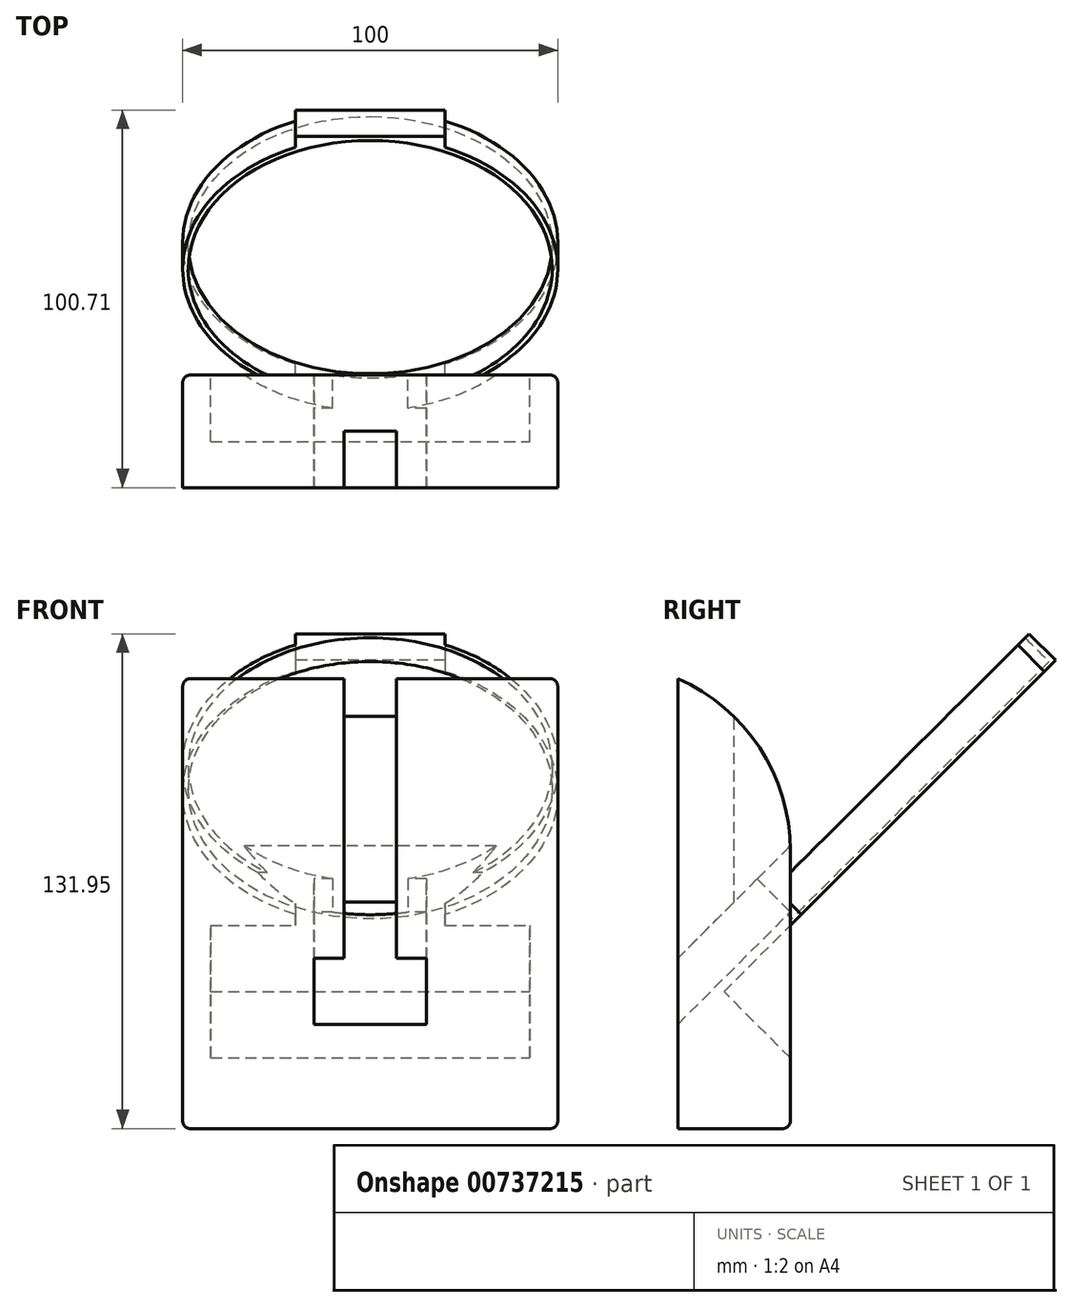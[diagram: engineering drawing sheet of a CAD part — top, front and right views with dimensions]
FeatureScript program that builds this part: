
annotation { "Feature Type Name" : "Feature", "Feature Type Description" : "" }
export const myFeature = defineFeature(function(context is Context, id is Id, definition is map)
    precondition{}
    {
        {
            var Q0;
            Q0=qCreatedBy(makeId("Front.planeOp"),FACE);
            var sketch = newSketch(context, id + "F0", { "sketchPlane" : qUnion([Q0])});
            skLineSegment(sketch, "E0.bottom", {"start": v(50, -60) * mm, "end": v(-50, -60) * mm});
            skLineSegment(sketch, "E0.top", {"start": v(50, 60) * mm, "end": v(-50, 60) * mm});
            skLineSegment(sketch, "E0.left", {"start": v(50, -60) * mm, "end": v(50, 60) * mm});
            skLineSegment(sketch, "E0.right", {"start": v(-50, -60) * mm, "end": v(-50, 60) * mm});
            skPoint(sketch, "E0.middle", {"position": v(0, 0) * mm});
            skSolve(sketch);
        }
        {
            var Q0;
            Q0 = qSketchRegion(id + "F0", true);
            extrude(context, id + "F1", {"entities" : qUnion([Q0]), "depth" : 30 * mm, "offsetDistance" : 25 * mm});
        }
        {
            var Q0;
            Q0=qCreatedBy(makeId("Right.planeOp"),FACE);
            var sketch = newSketch(context, id + "F2", { "sketchPlane" : qUnion([Q0])});
            skLineSegment(sketch, "E1", {"start": v(0, 8.31) * mm, "end": v(63.64, 71.95) * mm});
            skLineSegment(sketch, "E2", {"start": v(63.64, 71.95) * mm, "end": v(70.71, 64.88) * mm});
            skLineSegment(sketch, "E3", {"start": v(70.71, 64.88) * mm, "end": v(0, -5.83) * mm});
            skLineSegment(sketch, "E4", {"start": v(0, -5.83) * mm, "end": v(0, 8.31) * mm});
            skLineSegment(sketch, "E5", {"start": v(0, -5.83) * mm, "end": v(-17.68, -23.5) * mm});
            skLineSegment(sketch, "E6", {"start": v(-17.68, -23.5) * mm, "end": v(0, -41.19) * mm});
            skLineSegment(sketch, "E7", {"start": v(0, -41.19) * mm, "end": v(0, -5.83) * mm});
            skSolve(sketch);
        }
        {
            var Q0;
            Q0=makeQuery(id+"F2.imprint","IMPRINT",FACE,{"disambiguationData":[TD([[makeQuery(id+"F2.imprint","IMPRINT",EDGE,{"derivedFrom":sQuery(id+"F2.wireOp",EDGE,"E1")}),-1.0]])]});
            extrude(context, id + "F3", {"entities" : qUnion([Q0]), "operationType" : NewBodyOperationType.ADD, "endBound" : BoundingType.SYMMETRIC, "depth" : 40 * mm, "offsetDistance" : 25 * mm});
        }
        {
            var Q0;
            Q0=qCreatedBy(makeId("Right.planeOp"),FACE);
            var sketch = newSketch(context, id + "F4", { "sketchPlane" : qUnion([Q0])});
            skLineSegment(sketch, "E8", {"start": v(0, -41.19) * mm, "end": v(-17.68, -23.5) * mm});
            skLineSegment(sketch, "E9", {"start": v(-17.68, -23.5) * mm, "end": v(0, -5.83) * mm});
            skLineSegment(sketch, "E10", {"start": v(0, -5.83) * mm, "end": v(0, -41.19) * mm});
            skSolve(sketch);
        }
        {
            var Q0;
            Q0 = qSketchRegion(id + "F4", true);
            extrude(context, id + "F5", {"entities" : qUnion([Q0]), "operationType" : NewBodyOperationType.REMOVE, "endBound" : BoundingType.SYMMETRIC, "oppositeDirection" : true, "depth" : 85 * mm, "offsetDistance" : 25 * mm});
        }
        {
            var Q0;
            Q0=makeQuery(id+"F5.boolean.opBoolean","MERGE",FACE,{"derivedFrom":[makeQuery(id+"F3.opExtrude","SWEPT_FACE",FACE,{"disambiguationData":[OSD([sQuery(id+"F2.wireOp",EDGE,"E3")])]}),makeQuery(id+"F5.opExtrude","SWEPT_FACE",FACE,{"disambiguationData":[OSD([sQuery(id+"F4.wireOp",EDGE,"E9")])]})]});
            var sketch = newSketch(context, id + "F6", { "sketchPlane" : qUnion([Q0])});
            skCircle(sketch, "E11", {"center": v(0, 45.88) * mm, "radius": 50 * mm});
            skSolve(sketch);
        }
        {
            var Q0;
            Q0 = qSketchRegion(id + "F6", true);
            extrude(context, id + "F7", {"entities" : qUnion([Q0]), "operationType" : NewBodyOperationType.ADD, "oppositeDirection" : true, "depth" : 10 * mm, "offsetDistance" : 25 * mm});
        }
        {
            var Q0;
            Q0=makeQuery(id+"F7.boolean.opBoolean","MERGE",FACE,{"derivedFrom":[makeQuery(id+"F5.boolean.opBoolean","MERGE",FACE,{"derivedFrom":[makeQuery(id+"F3.opExtrude","SWEPT_FACE",FACE,{"disambiguationData":[OSD([sQuery(id+"F2.wireOp",EDGE,"E3")])]}),makeQuery(id+"F5.opExtrude","SWEPT_FACE",FACE,{"disambiguationData":[OSD([sQuery(id+"F4.wireOp",EDGE,"E9")])]})]}),makeQuery(id+"F7.opExtrude","CAP_FACE",FACE,{"disambiguationData":[OSD([sQuery(id+"F6.wireOp",EDGE,"E11")])],"isStart":true})]});
            var sketch = newSketch(context, id + "F8", { "sketchPlane" : qUnion([Q0])});
            skCircle(sketch, "E12", {"center": v(0, 45.88) * mm, "radius": 48.5 * mm});
            skSolve(sketch);
        }
        {
            var Q0;
            Q0 = qSketchRegion(id + "F8", true);
            extrude(context, id + "F9", {"entities" : qUnion([Q0]), "operationType" : NewBodyOperationType.REMOVE, "oppositeDirection" : true, "depth" : 15 * mm, "offsetDistance" : 25 * mm});
        }
        {
            var Q0;
            Q0=makeQuery(id+"F7.boolean.opBoolean","MERGE",FACE,{"derivedFrom":[makeQuery(id+"F5.boolean.opBoolean","MERGE",FACE,{"derivedFrom":[makeQuery(id+"F3.opExtrude","SWEPT_FACE",FACE,{"disambiguationData":[OSD([sQuery(id+"F2.wireOp",EDGE,"E3")])]}),makeQuery(id+"F5.opExtrude","SWEPT_FACE",FACE,{"disambiguationData":[OSD([sQuery(id+"F4.wireOp",EDGE,"E9")])]})]}),makeQuery(id+"F7.opExtrude","CAP_FACE",FACE,{"disambiguationData":[OSD([sQuery(id+"F6.wireOp",EDGE,"E11")])],"isStart":true})]});
            var sketch = newSketch(context, id + "F10", { "sketchPlane" : qUnion([Q0])});
            skCircle(sketch, "E13", {"center": v(0, 45.88) * mm, "radius": 50 * mm});
            skSolve(sketch);
        }
        {
            var Q0;
            Q0 = qSketchRegion(id + "F10", true);
            extrude(context, id + "F11", {"entities" : qUnion([Q0]), "operationType" : NewBodyOperationType.ADD, "oppositeDirection" : true, "depth" : 1 * mm, "offsetDistance" : 25 * mm});
        }
        {
            var Q0;
            Q0=makeQuery(id+"F1.opExtrude","CAP_EDGE",EDGE,{"disambiguationData":[OSD([sQuery(id+"F0.wireOp",EDGE,"E0.top")])],"isStart":true});
            fillet(context, id + "F12", {"entities" : qUnion([Q0]), "radius" : 50 * mm, "tangentPropagation" : true, "allowEdgeOverflow" : false});
        }
        {
            var Q0;
            Q0=qCreatedBy(makeId("Right.planeOp"),FACE);
            var sketch = newSketch(context, id + "F13", { "sketchPlane" : qUnion([Q0])});
            skLineSegment(sketch, "E14", {"start": v(-30, -32.24) * mm, "end": v(0, -2.24) * mm});
            skLineSegment(sketch, "E15", {"start": v(0, -2.24) * mm, "end": v(-8.8, 6.57) * mm});
            skLineSegment(sketch, "E16", {"start": v(-8.8, 6.57) * mm, "end": v(-30, -14.62) * mm});
            skLineSegment(sketch, "E17", {"start": v(-30, -14.62) * mm, "end": v(-30, -32.24) * mm});
            skSolve(sketch);
        }
        {
            var Q0;
            Q0 = qSketchRegion(id + "F13", true);
            extrude(context, id + "F14", {"entities" : qUnion([Q0]), "operationType" : NewBodyOperationType.REMOVE, "endBound" : BoundingType.SYMMETRIC, "depth" : 30 * mm, "offsetDistance" : 25 * mm});
        }
        {
            var Q0;
            Q0=makeQuery(id+"F1.opExtrude","CAP_FACE",FACE,{"disambiguationData":[OSD([sQuery(id+"F0.wireOp",EDGE,"E0.bottom"),sQuery(id+"F0.wireOp",EDGE,"E0.top"),sQuery(id+"F0.wireOp",EDGE,"E0.left"),sQuery(id+"F0.wireOp",EDGE,"E0.right")])],"isStart":false});
            var sketch = newSketch(context, id + "F15", { "sketchPlane" : qUnion([Q0])});
            skLineSegment(sketch, "E18.bottom", {"start": v(-7, -14.62) * mm, "end": v(7, -14.62) * mm});
            skLineSegment(sketch, "E18.top", {"start": v(-7, 60) * mm, "end": v(7, 60) * mm});
            skLineSegment(sketch, "E18.left", {"start": v(-7, -14.62) * mm, "end": v(-7, 60) * mm});
            skLineSegment(sketch, "E18.right", {"start": v(7, -14.62) * mm, "end": v(7, 60) * mm});
            skSolve(sketch);
        }
        {
            var Q0;
            Q0 = qSketchRegion(id + "F15", true);
            extrude(context, id + "F16", {"entities" : qUnion([Q0]), "operationType" : NewBodyOperationType.REMOVE, "oppositeDirection" : true, "depth" : 15 * mm, "offsetDistance" : 25 * mm});
        }
        {
            var Q0;
            Q0=makeQuery(id+"F1.opExtrude","CAP_EDGE",EDGE,{"disambiguationData":[OSD([sQuery(id+"F0.wireOp",EDGE,"E0.left")])],"isStart":true});
            var Q1;
            Q1=makeQuery(id+"F1.opExtrude","CAP_EDGE",EDGE,{"disambiguationData":[OSD([sQuery(id+"F0.wireOp",EDGE,"E0.bottom")])],"isStart":true});
            var Q2;
            Q2=makeQuery(id+"F1.opExtrude","SWEPT_EDGE",EDGE,{"disambiguationData":[OSD([sQuery(id+"F0.wireOp",EDGE,"E0.bottom"),sQuery(id+"F0.wireOp",EDGE,"E0.left")])]});
            var Q3;
            Q3=makeQuery(id+"F1.opExtrude","CAP_EDGE",EDGE,{"disambiguationData":[OSD([sQuery(id+"F0.wireOp",EDGE,"E0.right")])],"isStart":true});
            var Q4;
            Q4=makeQuery(id+"F1.opExtrude","SWEPT_EDGE",EDGE,{"disambiguationData":[OSD([sQuery(id+"F0.wireOp",EDGE,"E0.bottom"),sQuery(id+"F0.wireOp",EDGE,"E0.right")])]});
            fillet(context, id + "F17", {"entities" : qUnion([Q0, Q1, Q2, Q3, Q4]), "radius" : 2 * mm, "tangentPropagation" : true, "allowEdgeOverflow" : false});
        }
    });
